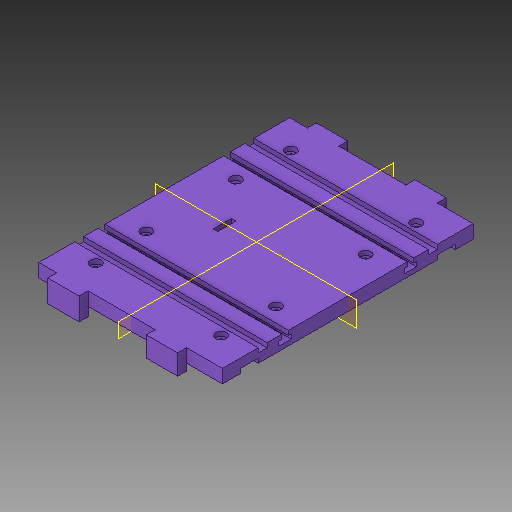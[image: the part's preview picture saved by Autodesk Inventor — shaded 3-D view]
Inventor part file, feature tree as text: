
AUTODESK INVENTOR PART (.ipt)
format: ipt  version: 2019 (Build 230136000, 136)  size: 311,808 bytes
history: native  units: in
note: dims shown in document units (in); Inventor stores cm internally (conversion verified against a paired STEP export)
features: extrude x12, sketch x11, mirror x10, plane x1
ambient origin geometry x8: Origin, YZ Plane, XZ Plane, XY Plane, X Axis, Y Axis, Z Axis, Center Point
bodies: Solid1 (feature_tree)
feature tree (34):
  extrude  "Extrusion1"  Depth=0.375in
  extrude  "Extrusion2"  Depth=0.75in
  mirror  "Mirror1"
  extrude  "Extrusion3"  Depth=14.0in TaperAngle=0.0deg
  extrude  "Extrusion4"  Depth=0.5in TaperAngle=0.0deg
  mirror  "Mirror2"
  extrude  "Extrusion5"  Depth=0.25in
  mirror  "Mirror3"
  extrude  "Extrusion8"  Depth=1.0in TaperAngle=0.0deg
  mirror  "Mirror4"
  plane  "Work Plane1"
  extrude  "Extrusion9"  Depth=1.25in
  mirror  "Mirror5"
  extrude  "Extrusion10"  Depth=0.5in TaperAngle=0.0deg
  mirror  "Mirror6"
  extrude  "Extrusion11"  Depth=0.25in
  extrude  "Extrusion12"  Depth=0.5in TaperAngle=0.0deg
  mirror  "Mirror7"
  mirror  "Mirror8"
  extrude  "Extrusion13"  Depth=0.25in
  extrude  "Extrusion14"  Depth=0.25in
  mirror  "Mirror9"
  mirror  "Mirror10"
  sketch  "Sketch4"  dims[d0=0.375in d1=0.375in]
  sketch  "Sketch6"  dims[d6=2.5in d8=0.75in]
  sketch  "Sketch7"  dims[d9=7.0in d10=14.0in d11=0.0in]
  sketch  "Sketch9"  dims[d12=0.875in d13=0.5in d14=0.0in]
  sketch  "Sketch12"  dims[d16=0.5in d18=0.25in]
  sketch  "Sketch13"  dims[d19=3.5in d20=1.0in d21=0.0in]
  sketch  "Sketch14"  dims[d22=1.75in d23=1.25in]
  sketch  "Sketch16"  dims[d24=1.0in d25=0.5in d26=0.0in]
  sketch  "Sketch17"  dims[d28=0.5in d29=0.25in]
  sketch  "Sketch18"  dims[d30=2.0in d31=0.5in d32=0.0in]
  sketch  "Sketch19"  dims[d46=3.5in d47=0.1875in d48=0.25in d49=0.25in d50=0.344in d51=0.5in d52=0.0in d53=-5.125in d54=1.0in d55=0.25in d56=1.0in d57=10.25in d58=0.0in d59=1.0in d60=0.25in d61=1.0in d62=9.0in d63=0.0in d71=0.266in d72=2.0in d73=0.5in d74=9.0in d75=0.0in d76=0.6in d77=0.25in d78=0.0in d79=0.266in d80=1.0in d81=0.25in d82=0.0in d83=0.6in d84=0.25in d85=0.0in]
